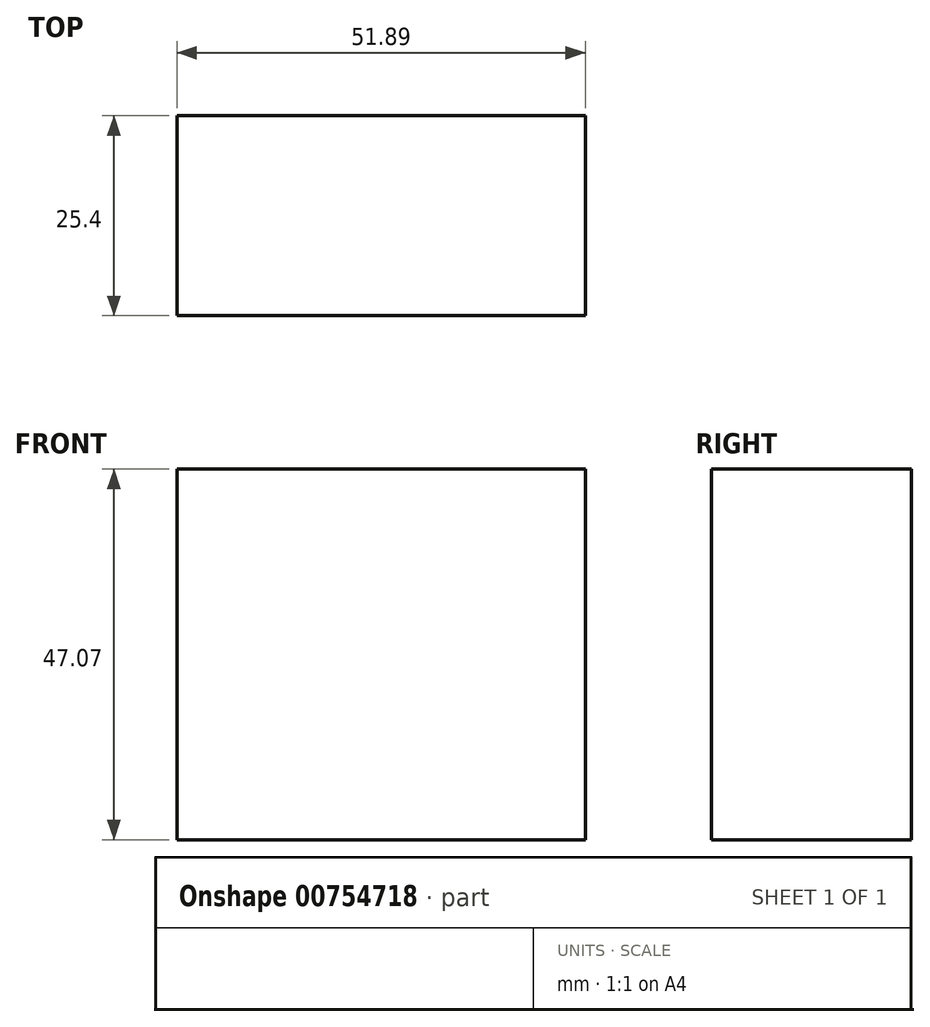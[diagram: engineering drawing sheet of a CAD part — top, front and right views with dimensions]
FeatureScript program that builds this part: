
annotation { "Feature Type Name" : "Feature", "Feature Type Description" : "" }
export const myFeature = defineFeature(function(context is Context, id is Id, definition is map)
    precondition{}
    {
        {
            var Q0;
            Q0=qCreatedBy(makeId("Front.planeOp"),FACE);
            var sketch = newSketch(context, id + "F0", { "sketchPlane" : qUnion([Q0])});
            skLineSegment(sketch, "E0.bottom", {"start": v(0, 0) * mm, "end": v(-51.89, 0) * mm});
            skLineSegment(sketch, "E0.top", {"start": v(0, 47.07) * mm, "end": v(-51.89, 47.07) * mm});
            skLineSegment(sketch, "E0.left", {"start": v(0, 0) * mm, "end": v(0, 47.07) * mm});
            skLineSegment(sketch, "E0.right", {"start": v(-51.89, 0) * mm, "end": v(-51.89, 47.07) * mm});
            skSolve(sketch);
        }
        {
            var Q0;
            Q0 = qSketchRegion(id + "F0", true);
            extrude(context, id + "F1", {"entities" : qUnion([Q0]), "depth" : 25.4 * mm, "offsetDistance" : 25.4 * mm});
        }
    });
